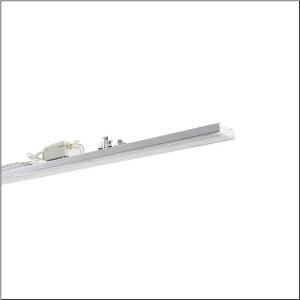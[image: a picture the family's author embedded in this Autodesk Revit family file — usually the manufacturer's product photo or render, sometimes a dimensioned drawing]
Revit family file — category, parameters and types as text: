
# Revit family: licross_21_recessed_mo_52te12dv4dxg
name_source: partatom
category: Lighting Fixtures
units: mm (PartAtom-declared; Revit-internal decimal feet)

## family parameters
Cut with Voids When Loaded = No
Host = Face
Light Source = No
Part Type = Normal
Room Calculation Point = No
Round Connector Dimension = Use Diameter
Shared = No

## types (1)
- --- (1 x LED, 13000 lm, 71 W, 4000K)
    Apparent Load = 71 VA
    CIE Flux Codes = 72 92 99 100 100
    Color Rendering = 80
    Color Temperature = 4000K
    Default Elevation = 1800 mm
    Description = Licross 21 Recessed MO, luminaire insert, of sheet steel, galvanised, coil coated, white, length: 2.250mm, width: 66mm, height: 67mm, LED rated luminous flux: 13.000lm, light colour: 840, SDCM (Standard Deviation of Colour Matching)MacAdam ≤ 3 SDCM (initial), control gear: DALI 2, with plug, 5-pole, with phase selection, mains connection: 220..240V, AC, 50/60Hz, rated input power: 71W, internal wiring halogen-free, primary optical cover: cover, of PMMA, light emission: direct distribution, primary light characteristic: symmetric, protection rating (complete): IP54, insulation class (complete): insulation class I (protective earthing), certification: CE, ENEC, VDE, UKCA, protection symbol: D if used in an environment with non-conductive dust loads with corresponding accessories, impact resistance: IK06, permissible ambient temperature for indoor applications: -25..+35°C, corresponds to IFS (International Featured Standards) requirements for safety and quality in the food industry, reducing of maximum allowable ambient temperature of 5°C with ceiling mounting, LABS conformity tested according to VDMA 24364:2018-05, The light source and the operating device comply with the requirements of the Ecodesign Regulation (EU) 2019/2020 and are replaceable in accordance with this regulation, packaging unit: 1 piece
    Height = 58 mm
    Lamp = 1 x LED
    Lamp Light Flux = 13000 lm
    Lamp Power = 71 W
    Lamp count = 1
    Length = 2250 mm
    Luminous efficacy = 183 lm/W
    Manufacturer = Siteco
    ModVariant = No
    Model = 52TE12DV4DXG
    Mounting Place = Ceiling
    Mounting Type = Pendant
    Number of Poles = 1
    OnlyDefault = Yes
    Power Factor = 1
    Product Name = Licross 21 Recessed MO
    Product group = luminaire insert | ceiling pendant
    ProductGroupID = 901
    Protection Class = Protection class I
    Protection Degree = IP 54
    RLX_Detail_Level = 1
    RLX_Emergency_Light_Flux = 0 lm
    RLX_Emergency_Type = 0
    RLX_Emergency_Type_DB = No
    RlxData = <blob elided: 29741 chars, md5=8bef415d>
    Socket = socket
    Standby Power = 0 W
    System Light Flux = 13000 lm
    System Power = 71 W
    Type Comments = factory setting: luminous flux: 100 % | dim-lin: 254 | 324 mA
    Type Image = l_1296930.jpg
    URL = http://relux.com
    VarID = @adj_128093
    Voltage = 0 V
    Weight = 0.00 kg
    Width = 66 mm

## geometry (parser evidence)
native form markers: Blend x4, Sweep x10
no freeform markers — native parametric forms only
